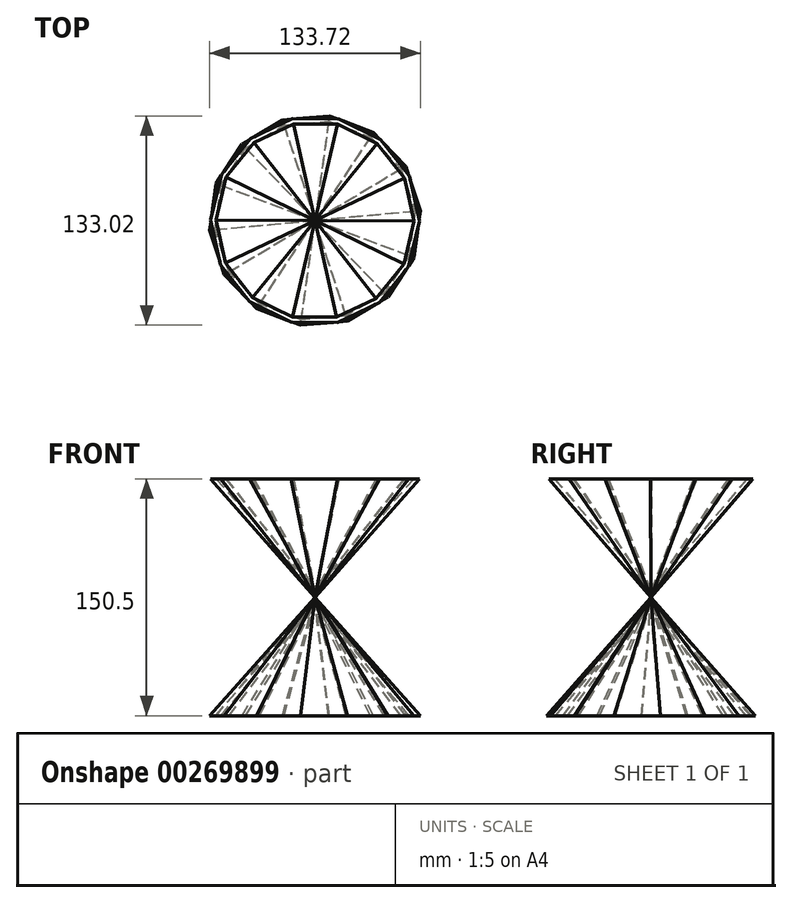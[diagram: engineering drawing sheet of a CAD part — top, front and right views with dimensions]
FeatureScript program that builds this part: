
annotation { "Feature Type Name" : "Feature", "Feature Type Description" : "" }
export const myFeature = defineFeature(function(context is Context, id is Id, definition is map)
    precondition{}
    {
        {
            var Q0;
            Q0=qCreatedBy(makeId("Top.planeOp"),FACE);
            cPlane(context, id + "F0", {"entities" : qUnion([Q0]), "cplaneType" : CPlaneType.OFFSET, "offset" : 75.5 * mm, "width" : 152.4 * mm, "height" : 152.4 * mm});
        }
        {
            var Q0;
            Q0=qCreatedBy(id+"F0.planeOp",FACE);
            var sketch = newSketch(context, id + "F1", { "sketchPlane" : qUnion([Q0])});
            skCircle(sketch, "E0.cCircle", {"center": v(0, 0) * mm, "radius": 64.56 * mm, "construction": true});
            skLineSegment(sketch, "E0.0", {"start": v(-59.47, 29.14) * mm, "end": v(-40.94, 52.05) * mm});
            skLineSegment(sketch, "E0.1", {"start": v(-40.94, 52.05) * mm, "end": v(-14.3, 64.66) * mm});
            skLineSegment(sketch, "E0.2", {"start": v(-14.3, 64.66) * mm, "end": v(15.17, 64.46) * mm});
            skLineSegment(sketch, "E0.3", {"start": v(15.17, 64.46) * mm, "end": v(41.64, 51.5) * mm});
            skLineSegment(sketch, "E0.4", {"start": v(41.64, 51.5) * mm, "end": v(59.86, 28.33) * mm});
            skLineSegment(sketch, "E0.5", {"start": v(59.86, 28.33) * mm, "end": v(66.22, -0.45) * mm});
            skLineSegment(sketch, "E0.6", {"start": v(66.22, -0.45) * mm, "end": v(59.47, -29.14) * mm});
            skLineSegment(sketch, "E0.7", {"start": v(59.47, -29.14) * mm, "end": v(40.94, -52.05) * mm});
            skLineSegment(sketch, "E0.8", {"start": v(40.94, -52.05) * mm, "end": v(14.3, -64.66) * mm});
            skLineSegment(sketch, "E0.9", {"start": v(14.3, -64.66) * mm, "end": v(-15.17, -64.46) * mm});
            skLineSegment(sketch, "E0.10", {"start": v(-15.17, -64.46) * mm, "end": v(-41.64, -51.5) * mm});
            skLineSegment(sketch, "E0.11", {"start": v(-41.64, -51.5) * mm, "end": v(-59.86, -28.33) * mm});
            skLineSegment(sketch, "E0.12", {"start": v(-59.86, -28.33) * mm, "end": v(-66.22, 0.45) * mm});
            skLineSegment(sketch, "E0.13", {"start": v(-66.22, 0.45) * mm, "end": v(-59.47, 29.14) * mm});
            skPoint(sketch, "E0.0.midPoint", {"position": v(-50.2, 40.6) * mm});
            skSolve(sketch);
        }
        {
            var Q0;
            Q0=makeQuery(id+"F1.imprint","IMPRINT",FACE,{"disambiguationData":[TD([[makeQuery(id+"F1.imprint","IMPRINT",EDGE,{"derivedFrom":sQuery(id+"F1.wireOp",EDGE,"E0.0")}),-1.0]])]});
            var Q1;
            Q1=qCreatedBy(makeId("Origin.pointOp"),VERTEX);
            loft(context, id + "F2", {"sheetProfilesArray" : [{ "sheetProfileEntities" : qUnion([Q0]) }, { "sheetProfileEntities" : qUnion([Q1]) }]});
        }
        {
            var Q0;
            Q0=makeQuery(id+"F2.opLoft","CAP_FACE",FACE,{"disambiguationData":[OSD([makeQuery(id+"F1.imprint","IMPRINT",FACE,{"disambiguationData":[TD([[makeQuery(id+"F1.imprint","IMPRINT",EDGE,{"derivedFrom":sQuery(id+"F1.wireOp",EDGE,"E0.0")}),-1.0]])]})])],"isStart":true});
            shell(context, id + "F3", {"entities" : qUnion([Q0]), "thickness" : 2.5 * mm});
        }
        {
            var Q0;
            Q0=qCreatedBy(makeId("Top.planeOp"),FACE);
            cPlane(context, id + "F4", {"entities" : qUnion([Q0]), "cplaneType" : CPlaneType.OFFSET, "offset" : 75 * mm, "oppositeDirection" : true, "width" : 150 * mm, "height" : 150 * mm});
        }
        {
            var Q0;
            Q0=qCreatedBy(id+"F4.planeOp",FACE);
            var sketch = newSketch(context, id + "F5", { "sketchPlane" : qUnion([Q0])});
            skCircle(sketch, "E1.cCircle", {"center": v(0, 0) * mm, "radius": 65.44 * mm, "construction": true});
            skLineSegment(sketch, "E1.0", {"start": v(-37.02, -55.99) * mm, "end": v(-57.65, -34.38) * mm});
            skLineSegment(sketch, "E1.1", {"start": v(-57.65, -34.38) * mm, "end": v(-66.86, -5.96) * mm});
            skLineSegment(sketch, "E1.2", {"start": v(-66.86, -5.96) * mm, "end": v(-62.82, 23.64) * mm});
            skLineSegment(sketch, "E1.3", {"start": v(-62.82, 23.64) * mm, "end": v(-46.35, 48.55) * mm});
            skLineSegment(sketch, "E1.4", {"start": v(-46.35, 48.55) * mm, "end": v(-20.7, 63.85) * mm});
            skLineSegment(sketch, "E1.5", {"start": v(-20.7, 63.85) * mm, "end": v(9.06, 66.5) * mm});
            skLineSegment(sketch, "E1.6", {"start": v(9.06, 66.5) * mm, "end": v(37.02, 55.99) * mm});
            skLineSegment(sketch, "E1.7", {"start": v(37.02, 55.99) * mm, "end": v(57.65, 34.38) * mm});
            skLineSegment(sketch, "E1.8", {"start": v(57.65, 34.38) * mm, "end": v(66.86, 5.96) * mm});
            skLineSegment(sketch, "E1.9", {"start": v(66.86, 5.96) * mm, "end": v(62.82, -23.64) * mm});
            skLineSegment(sketch, "E1.10", {"start": v(62.82, -23.64) * mm, "end": v(46.35, -48.55) * mm});
            skLineSegment(sketch, "E1.11", {"start": v(46.35, -48.55) * mm, "end": v(20.7, -63.85) * mm});
            skLineSegment(sketch, "E1.12", {"start": v(20.7, -63.85) * mm, "end": v(-9.06, -66.5) * mm});
            skLineSegment(sketch, "E1.13", {"start": v(-9.06, -66.5) * mm, "end": v(-37.02, -55.99) * mm});
            skPoint(sketch, "E1.0.midPoint", {"position": v(-47.34, -45.18) * mm});
            skSolve(sketch);
        }
        {
            var Q0;
            Q0=makeQuery(id+"F5.imprint","IMPRINT",FACE,{"disambiguationData":[TD([[makeQuery(id+"F5.imprint","IMPRINT",EDGE,{"derivedFrom":sQuery(id+"F5.wireOp",EDGE,"E1.0")}),-1.0]])]});
            var Q1;
            Q1=qCreatedBy(makeId("Origin.pointOp"),VERTEX);
            loft(context, id + "F6", {"sheetProfilesArray" : [{ "sheetProfileEntities" : qUnion([Q0]) }, { "sheetProfileEntities" : qUnion([Q1]) }]});
        }
        {
            var Q0;
            Q0=makeQuery(id+"F6.opLoft","CAP_FACE",FACE,{"disambiguationData":[OSD([makeQuery(id+"F5.imprint","IMPRINT",FACE,{"disambiguationData":[TD([[makeQuery(id+"F5.imprint","IMPRINT",EDGE,{"derivedFrom":sQuery(id+"F5.wireOp",EDGE,"E1.0")}),-1.0]])]})])],"isStart":true});
            shell(context, id + "F7", {"entities" : qUnion([Q0]), "thickness" : 2.5 * mm});
        }
        {
            var Q0;
            Q0=qCreatedBy(makeId("Right.planeOp"),FACE);
            var sketch = newSketch(context, id + "F8", { "sketchPlane" : qUnion([Q0])});
            skArc(sketch, "E2", {"start": v(0, -31.84) * mm, "mid": v(35.4, 3.56) * mm, "end": v(0, 38.96) * mm});
            skSolve(sketch);
        }
        {
            var Q0;
            Q0=qCreatedBy(makeId("Right.planeOp"),FACE);
            var sketch = newSketch(context, id + "F9", { "sketchPlane" : qUnion([Q0])});
            skLineSegment(sketch, "E3", {"start": v(0, 39.25) * mm, "end": v(0, -31.56) * mm});
            skSolve(sketch);
        }
        {
            var Q0;
            Q0=sQuery(id+"F8.wireOp",EDGE,"E2");
            var Q1;
            Q1=sQuery(id+"F9.wireOp",EDGE,"E3");
            revolve(context, id + "F10", {"bodyType" : ToolBodyType.SURFACE, "surfaceEntities" : qUnion([Q0]), "axis" : qUnion([Q1]), "revolveType" : RevolveType.FULL});
        }
    });
